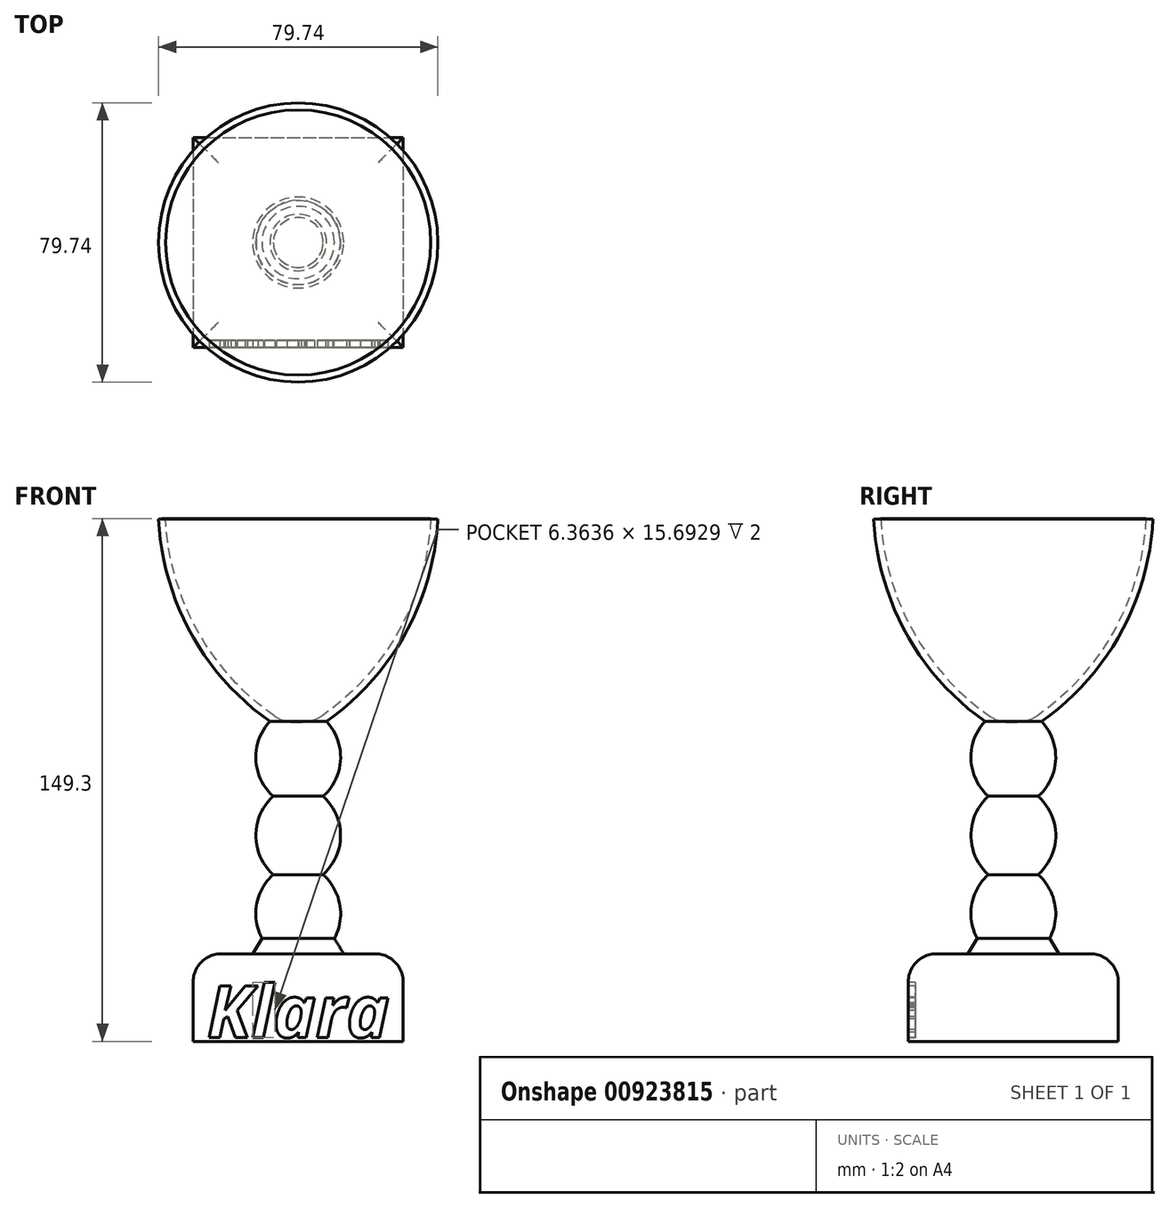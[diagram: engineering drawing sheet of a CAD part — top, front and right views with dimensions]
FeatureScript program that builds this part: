
annotation { "Feature Type Name" : "Feature", "Feature Type Description" : "" }
export const myFeature = defineFeature(function(context is Context, id is Id, definition is map)
    precondition{}
    {
        {
            var Q0;
            Q0=qCreatedBy(makeId("Top.planeOp"),FACE);
            var sketch = newSketch(context, id + "F0", { "sketchPlane" : qUnion([Q0])});
            skLineSegment(sketch, "E0.bottom", {"start": v(0, 0) * mm, "end": v(60, 0) * mm});
            skLineSegment(sketch, "E0.top", {"start": v(0, -60) * mm, "end": v(60, -60) * mm});
            skLineSegment(sketch, "E0.left", {"start": v(0, 0) * mm, "end": v(0, -60) * mm});
            skLineSegment(sketch, "E0.right", {"start": v(60, 0) * mm, "end": v(60, -60) * mm});
            skSolve(sketch);
        }
        {
            var Q0;
            Q0=makeQuery(id+"F0.imprint","IMPRINT",FACE,{"disambiguationData":[TD([[makeQuery(id+"F0.imprint","IMPRINT",EDGE,{"derivedFrom":sQuery(id+"F0.wireOp",EDGE,"E0.bottom")}),-1.0]])]});
            extrude(context, id + "F1", {"entities" : qUnion([Q0]), "depth" : 30 * mm, "offsetDistance" : 25 * mm});
        }
        {
            var Q0;
            Q0=makeQuery(id+"F1.opExtrude","SWEPT_BODY",BODY,{"disambiguationData":[OSD([sQuery(id+"F0.wireOp",EDGE,"E0.bottom"),sQuery(id+"F0.wireOp",EDGE,"E0.top"),sQuery(id+"F0.wireOp",EDGE,"E0.left"),sQuery(id+"F0.wireOp",EDGE,"E0.right")])]});
            transform(context, id + "F2", {"entities" : qUnion([Q0]), "transformType" : TransformType.TRANSLATION_3D, "dx" : -30 * mm, "dy" : 30 * mm, "dz" : 0 * mm, "makeCopy" : false});
        }
        {
            var Q0;
            Q0=qCreatedBy(makeId("Front.planeOp"),FACE);
            var sketch = newSketch(context, id + "F3", { "sketchPlane" : qUnion([Q0])});
            skArc(sketch, "E1", {"start": v(7.1, 30.27) * mm, "mid": v(12.1, 41.45) * mm, "end": v(7.1, 52.63) * mm});
            skArc(sketch, "E2", {"start": v(7.1, 52.63) * mm, "mid": v(12.1, 63.81) * mm, "end": v(7.1, 75) * mm});
            skArc(sketch, "E3", {"start": v(7.1, 75) * mm, "mid": v(12.1, 85.49) * mm, "end": v(8.09, 96.4) * mm});
            skLineSegment(sketch, "E4", {"start": v(0, 30.2) * mm, "end": v(0, 158.08) * mm});
            skLineSegment(sketch, "E5", {"start": v(7.1, 30.27) * mm, "end": v(7.1, 29.78) * mm});
            skLineSegment(sketch, "E6", {"start": v(7.1, 29.78) * mm, "end": v(0, 29.78) * mm});
            skLineSegment(sketch, "E7", {"start": v(0, 29.78) * mm, "end": v(0, 30.2) * mm});
            skArc(sketch, "E8", {"start": v(8.09, 96.4) * mm, "mid": v(30.66, 121.62) * mm, "end": v(39.87, 154.2) * mm});
            skLineSegment(sketch, "E9", {"start": v(37.87, 154.3) * mm, "end": v(39.87, 154.2) * mm});
            skLineSegment(sketch, "E10", {"start": v(0, 96.12) * mm, "end": v(1.06, 96.12) * mm});
            skArc(sketch, "E11.trimOffspring", {"start": v(6.8, 97.93) * mm, "mid": v(28.86, 122.52) * mm, "end": v(37.87, 154.3) * mm});
            skPoint(sketch, "E12.visualSharp", {"position": v(4.09, 96.12) * mm});
            skArc(sketch, "E12.filletArc", {"start": v(1.06, 96.12) * mm, "mid": v(4.07, 96.58) * mm, "end": v(6.8, 97.93) * mm});
            skSolve(sketch);
        }
        {
            var Q0;
            {var subQ10=sQuery(id+"F3.wireOp",EDGE,"I5DjJ9ts-EXyD-T3Ez-MTNL-TmspGHFE94tQ");Q0=makeQuery(id+"F3.imprint","IMPRINT",FACE,{"disambiguationData":[TD([[makeQuery(id+"F3.imprint","IMPRINT",EDGE,{"derivedFrom":subQ10}),1.0]])]});}
            var Q1;
            {var subQ0=sQuery(id+"F3.wireOp",EDGE,"E3");Q1=makeQuery(id+"F3.imprint","IMPRINT",FACE,{"disambiguationData":[TD([[makeQuery(id+"F3.imprint","IMPRINT",EDGE,{"derivedFrom":subQ0}),1.0]])]});}
            var Q2;
            {var subQ0=sQuery(id+"F3.wireOp",EDGE,"E2");Q2=makeQuery(id+"F3.imprint","IMPRINT",FACE,{"disambiguationData":[TD([[makeQuery(id+"F3.imprint","IMPRINT",EDGE,{"derivedFrom":subQ0}),1.0]])]});}
            var Q3;
            {var subQ0=sQuery(id+"F3.wireOp",EDGE,"E1");Q3=makeQuery(id+"F3.imprint","IMPRINT",FACE,{"disambiguationData":[TD([[makeQuery(id+"F3.imprint","IMPRINT",EDGE,{"derivedFrom":subQ0}),1.0]])]});}
            var Q4;
            Q4=sQuery(id+"F3.wireOp",EDGE,"E4");
            revolve(context, id + "F4", {"operationType" : NewBodyOperationType.ADD, "surfaceOperationType" : NewSurfaceOperationType.NEW, "entities" : qUnion([Q0, Q1, Q2, Q3]), "axis" : qUnion([Q4]), "revolveType" : RevolveType.FULL});
        }
        {
            var Q0;
            Q0=makeQuery(id+"F4.opRevolve","SWEPT_EDGE",EDGE,{"disambiguationData":[OSD([sQuery(id+"F3.wireOp",EDGE,"vcvWEaiL-wYzA-kxNN-2hgw-6SO7PC0KjmtI"),sQuery(id+"F3.wireOp",EDGE,"E1"),sQuery(id+"F3.wireOp",EDGE,"E5")])]});
            fillet(context, id + "F5", {"entities" : qUnion([Q0]), "radius" : 1 * mm, "tangentPropagation" : true, "allowEdgeOverflow" : false});
        }
        {
            var Q0;
            Q0=makeQuery(id+"F5.opFillet","BLEND_EDGE",EDGE,{"blendedFrom":[makeQuery(id+"F4.opRevolve","SWEPT_EDGE",EDGE,{"disambiguationData":[OSD([sQuery(id+"F3.wireOp",EDGE,"vcvWEaiL-wYzA-kxNN-2hgw-6SO7PC0KjmtI"),sQuery(id+"F3.wireOp",EDGE,"E1"),sQuery(id+"F3.wireOp",EDGE,"E5")])]}),makeQuery(id+"F1.opExtrude","CAP_FACE",FACE,{"disambiguationData":[OSD([sQuery(id+"F0.wireOp",EDGE,"E0.bottom"),sQuery(id+"F0.wireOp",EDGE,"E0.top"),sQuery(id+"F0.wireOp",EDGE,"E0.left"),sQuery(id+"F0.wireOp",EDGE,"E0.right")])],"isStart":false})],"blendedInto":[makeQuery(id+"F1.opExtrude","CAP_FACE",FACE,{"disambiguationData":[OSD([sQuery(id+"F0.wireOp",EDGE,"E0.bottom"),sQuery(id+"F0.wireOp",EDGE,"E0.top"),sQuery(id+"F0.wireOp",EDGE,"E0.left"),sQuery(id+"F0.wireOp",EDGE,"E0.right")])],"isStart":false})]});
            chamfer(context, id + "F6", {"entities" : qUnion([Q0]), "width" : 3 * mm, "tangentPropagation" : true});
        }
        {
            var Q0;
            Q0=makeQuery(id+"F1.opExtrude","CAP_EDGE",EDGE,{"disambiguationData":[OSD([sQuery(id+"F0.wireOp",EDGE,"E0.left")])],"isStart":false});
            var Q1;
            Q1=makeQuery(id+"F1.opExtrude","CAP_EDGE",EDGE,{"disambiguationData":[OSD([sQuery(id+"F0.wireOp",EDGE,"E0.bottom")])],"isStart":false});
            var Q2;
            Q2=makeQuery(id+"F1.opExtrude","CAP_EDGE",EDGE,{"disambiguationData":[OSD([sQuery(id+"F0.wireOp",EDGE,"E0.right")])],"isStart":false});
            var Q3;
            Q3=makeQuery(id+"F1.opExtrude","CAP_EDGE",EDGE,{"disambiguationData":[OSD([sQuery(id+"F0.wireOp",EDGE,"E0.top")])],"isStart":false});
            fillet(context, id + "F7", {"entities" : qUnion([Q0, Q1, Q2, Q3]), "radius" : 8 * mm, "tangentPropagation" : true, "allowEdgeOverflow" : false});
        }
        {
            var Q0;
            Q0=makeQuery(id+"F1.opExtrude","SWEPT_FACE",FACE,{"disambiguationData":[OSD([sQuery(id+"F0.wireOp",EDGE,"E0.top")])]});
            var sketch = newSketch(context, id + "F8", { "sketchPlane" : qUnion([Q0])});
            skText(sketch, "E13", { "text": "Klara", "fontName": "OpenSans-BoldItalic.ttf"});
            const initialGuessF8  = {"E13": [-0.026, 0.00613, 1, 0, 0.01487]};
            skSetInitialGuess(sketch, initialGuessF8);
            skSolve(sketch);
        }
        {
            var Q0;
            Q0=qSketchRegion(id+"F8",true);
            extrude(context, id + "F9", {"entities" : qUnion([Q0]), "operationType" : NewBodyOperationType.REMOVE, "oppositeDirection" : true, "depth" : 2 * mm, "offsetDistance" : 25 * mm});
        }
        {
            var Q0;
            Q0=makeQuery(id+"F1.opExtrude","CAP_FACE",FACE,{"disambiguationData":[OSD([sQuery(id+"F0.wireOp",EDGE,"E0.bottom"),sQuery(id+"F0.wireOp",EDGE,"E0.top"),sQuery(id+"F0.wireOp",EDGE,"E0.left"),sQuery(id+"F0.wireOp",EDGE,"E0.right")])],"isStart":true});
            extrude(context, id + "F10", {"entities" : qUnion([Q0]), "operationType" : NewBodyOperationType.REMOVE, "oppositeDirection" : true, "depth" : 5 * mm, "offsetDistance" : 25 * mm});
        }
    });
